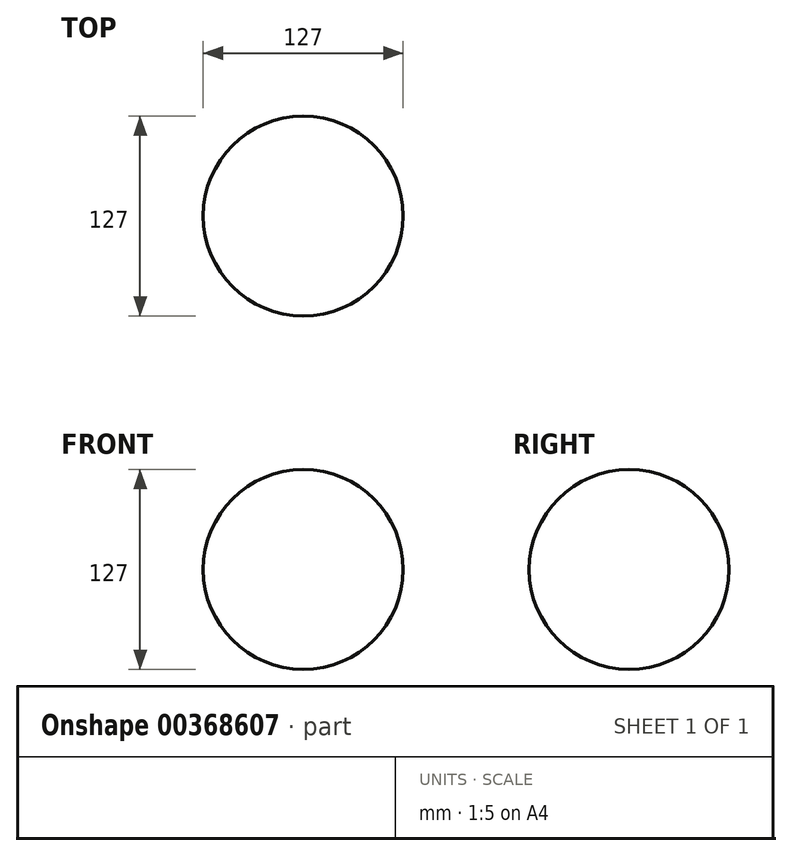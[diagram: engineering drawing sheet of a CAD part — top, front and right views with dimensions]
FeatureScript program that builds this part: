
annotation { "Feature Type Name" : "Feature", "Feature Type Description" : "" }
export const myFeature = defineFeature(function(context is Context, id is Id, definition is map)
    precondition{}
    {
        {
            var Q0;
            Q0=qCreatedBy(makeId("Front.planeOp"),FACE);
            var sketch = newSketch(context, id + "F0", { "sketchPlane" : qUnion([Q0])});
            skLineSegment(sketch, "E0", {"start": v(0, -63.5) * mm, "end": v(0, 63.5) * mm});
            skArc(sketch, "E1", {"start": v(0, -63.5) * mm, "mid": v(63.5, 0) * mm, "end": v(0, 63.5) * mm});
            skSolve(sketch);
        }
        {
            var Q0;
            Q0=makeQuery(id+"F0.imprint","IMPRINT",FACE,{"disambiguationData":[TD([[makeQuery(id+"F0.imprint","IMPRINT",EDGE,{"derivedFrom":sQuery(id+"F0.wireOp",EDGE,"E0")}),-1.0]])]});
            var Q1;
            Q1=sQuery(id+"F0.wireOp",EDGE,"E0");
            revolve(context, id + "F1", {"entities" : qUnion([Q0]), "axis" : qUnion([Q1]), "revolveType" : RevolveType.FULL});
        }
    });
